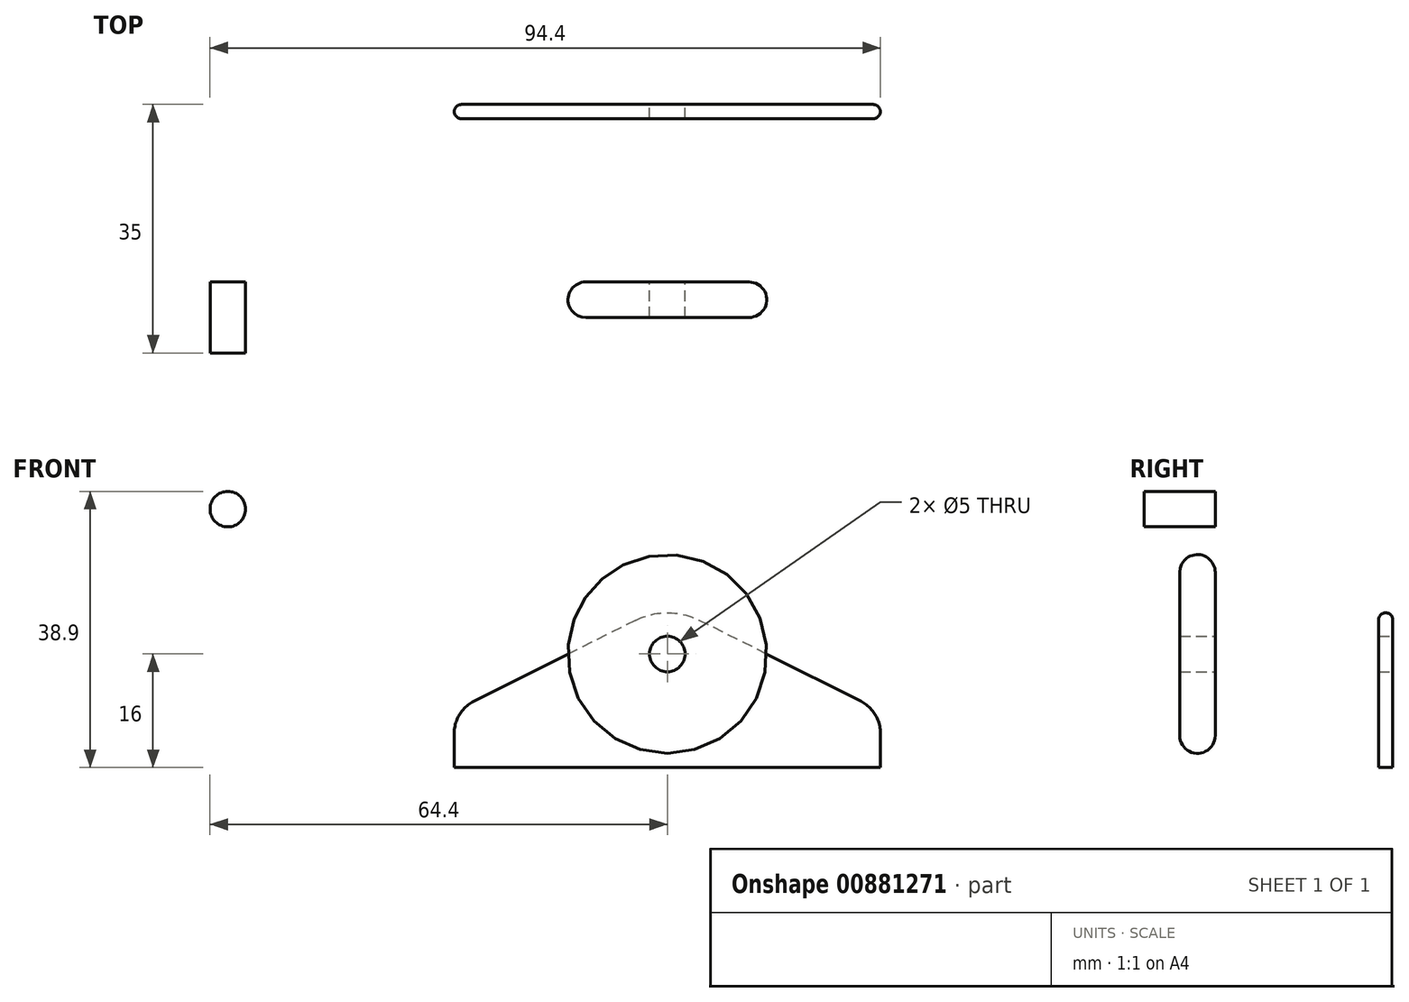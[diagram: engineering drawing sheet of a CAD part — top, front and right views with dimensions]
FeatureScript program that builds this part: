
annotation { "Feature Type Name" : "Feature", "Feature Type Description" : "" }
export const myFeature = defineFeature(function(context is Context, id is Id, definition is map)
    precondition{}
    {
        {
            var Q0;
            Q0=qCreatedBy(makeId("Front.planeOp"),FACE);
            var sketch = newSketch(context, id + "F0", { "sketchPlane" : qUnion([Q0])});
            skLineSegment(sketch, "E0", {"start": v(0, 0) * mm, "end": v(30, 0) * mm});
            skLineSegment(sketch, "E1", {"start": v(30, 0) * mm, "end": v(30, 4.86) * mm});
            skLineSegment(sketch, "E2", {"start": v(27.24, 9.33) * mm, "end": v(4.48, 20.75) * mm});
            skLineSegment(sketch, "E3.MirrorCS", {"start": v(-27.24, 9.33) * mm, "end": v(-4.48, 20.75) * mm});
            skLineSegment(sketch, "E4.MirrorCS", {"start": v(0, 0) * mm, "end": v(-30, 0) * mm});
            skLineSegment(sketch, "E5.MirrorCS", {"start": v(-30, 0) * mm, "end": v(-30, 4.86) * mm});
            skPoint(sketch, "E6.visualSharp", {"position": v(0, 23) * mm});
            skArc(sketch, "E6.filletArc", {"start": v(4.48, 20.75) * mm, "mid": v(0, 21.81) * mm, "end": v(-4.48, 20.75) * mm});
            skPoint(sketch, "E7.visualSharp", {"position": v(-30, 7.95) * mm});
            skArc(sketch, "E7.filletArc", {"start": v(-27.24, 9.33) * mm, "mid": v(-29.26, 7.49) * mm, "end": v(-30, 4.86) * mm});
            skPoint(sketch, "E8.visualSharp", {"position": v(30, 7.95) * mm});
            skArc(sketch, "E8.filletArc", {"start": v(30, 4.86) * mm, "mid": v(29.26, 7.49) * mm, "end": v(27.24, 9.33) * mm});
            skCircle(sketch, "E9", {"center": v(0, 16) * mm, "radius": 2.5 * mm});
            skSolve(sketch);
        }
        {
            var Q0;
            Q0 = qSketchRegion(id + "F0", true);
            extrude(context, id + "F1", {"entities" : qUnion([Q0]), "depth" : 2 * mm, "offsetDistance" : 25 * mm});
        }
        {
            var Q0;
            Q0=makeQuery(id+"F1.opExtrude","CAP_EDGE",EDGE,{"disambiguationData":[OSD([sQuery(id+"F0.wireOp",EDGE,"E3.MirrorCS")])],"isStart":true});
            var Q1;
            Q1=makeQuery(id+"F1.opExtrude","CAP_EDGE",EDGE,{"disambiguationData":[OSD([sQuery(id+"F0.wireOp",EDGE,"E5.MirrorCS")])],"isStart":true});
            var Q2;
            Q2=makeQuery(id+"F1.opExtrude","CAP_EDGE",EDGE,{"disambiguationData":[OSD([sQuery(id+"F0.wireOp",EDGE,"E7.filletArc")])],"isStart":true});
            var Q3;
            Q3=makeQuery(id+"F1.opExtrude","CAP_EDGE",EDGE,{"disambiguationData":[OSD([sQuery(id+"F0.wireOp",EDGE,"E2")])],"isStart":true});
            var Q4;
            Q4=makeQuery(id+"F1.opExtrude","CAP_EDGE",EDGE,{"disambiguationData":[OSD([sQuery(id+"F0.wireOp",EDGE,"E8.filletArc")])],"isStart":true});
            var Q5;
            Q5=makeQuery(id+"F1.opExtrude","CAP_EDGE",EDGE,{"disambiguationData":[OSD([sQuery(id+"F0.wireOp",EDGE,"E1")])],"isStart":true});
            var Q6;
            Q6=makeQuery(id+"F1.opExtrude","CAP_EDGE",EDGE,{"disambiguationData":[OSD([sQuery(id+"F0.wireOp",EDGE,"E2")])],"isStart":false});
            var Q7;
            Q7=makeQuery(id+"F1.opExtrude","CAP_EDGE",EDGE,{"disambiguationData":[OSD([sQuery(id+"F0.wireOp",EDGE,"E8.filletArc")])],"isStart":false});
            var Q8;
            Q8=makeQuery(id+"F1.opExtrude","CAP_EDGE",EDGE,{"disambiguationData":[OSD([sQuery(id+"F0.wireOp",EDGE,"E1")])],"isStart":false});
            var Q9;
            Q9=makeQuery(id+"F1.opExtrude","CAP_EDGE",EDGE,{"disambiguationData":[OSD([sQuery(id+"F0.wireOp",EDGE,"E6.filletArc")])],"isStart":true});
            var Q10;
            Q10=makeQuery(id+"F1.opExtrude","CAP_EDGE",EDGE,{"disambiguationData":[OSD([sQuery(id+"F0.wireOp",EDGE,"E6.filletArc")])],"isStart":false});
            var Q11;
            Q11=makeQuery(id+"F1.opExtrude","CAP_EDGE",EDGE,{"disambiguationData":[OSD([sQuery(id+"F0.wireOp",EDGE,"E3.MirrorCS")])],"isStart":false});
            var Q12;
            Q12=makeQuery(id+"F1.opExtrude","CAP_EDGE",EDGE,{"disambiguationData":[OSD([sQuery(id+"F0.wireOp",EDGE,"E7.filletArc")])],"isStart":false});
            var Q13;
            Q13=makeQuery(id+"F1.opExtrude","CAP_EDGE",EDGE,{"disambiguationData":[OSD([sQuery(id+"F0.wireOp",EDGE,"E5.MirrorCS")])],"isStart":false});
            fillet(context, id + "F2", {"entities" : qUnion([Q0, Q1, Q2, Q3, Q4, Q5, Q6, Q7, Q8, Q9, Q10, Q11, Q12, Q13]), "radius" : 1 * mm, "tangentPropagation" : true, "allowEdgeOverflow" : false});
        }
        {
            var Q0;
            Q0=qCreatedBy(makeId("Front.planeOp"),FACE);
            cPlane(context, id + "F3", {"entities" : qUnion([Q0]), "cplaneType" : CPlaneType.OFFSET, "offset" : 25 * mm, "width" : 150 * mm, "height" : 150 * mm});
        }
        {
            var Q0;
            Q0=qCreatedBy(id+"F3.planeOp",FACE);
            var sketch = newSketch(context, id + "F4", { "sketchPlane" : qUnion([Q0])});
            skCircle(sketch, "E10", {"center": v(0, 16) * mm, "radius": 14 * mm});
            skCircle(sketch, "E11", {"center": v(0, 16) * mm, "radius": 2.5 * mm});
            skSolve(sketch);
        }
        {
            var Q0;
            Q0 = qSketchRegion(id + "F4", true);
            extrude(context, id + "F5", {"entities" : qUnion([Q0]), "depth" : 5 * mm, "offsetDistance" : 25 * mm});
        }
        {
            var Q0;
            Q0=qCreatedBy(id+"F3.planeOp",FACE);
            var sketch = newSketch(context, id + "F6", { "sketchPlane" : qUnion([Q0])});
            skCircle(sketch, "E12", {"center": v(-61.9, 36.4) * mm, "radius": 2.5 * mm});
            skSolve(sketch);
        }
        {
            var Q0;
            Q0 = qSketchRegion(id + "F6", true);
            extrude(context, id + "F7", {"entities" : qUnion([Q0]), "depth" : 10 * mm, "offsetDistance" : 25 * mm});
        }
        {
            var Q0;
            Q0=makeQuery(id+"F5.opExtrude","SWEPT_FACE",FACE,{"disambiguationData":[OSD([sQuery(id+"F4.wireOp",EDGE,"E10")])]});
            fillet(context, id + "F8", {"entities" : qUnion([Q0]), "radius" : 2.5 * mm, "tangentPropagation" : true, "allowEdgeOverflow" : false});
        }
    });
